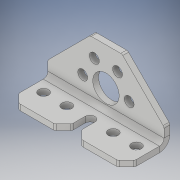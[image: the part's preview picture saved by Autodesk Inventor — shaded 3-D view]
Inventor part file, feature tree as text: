
AUTODESK INVENTOR PART (.ipt)
format: ipt  version: 2018 (Build 220112000, 112)  size: 153,600 bytes
history: native  units: in
note: dims shown in document units (in); Inventor stores cm internally (conversion verified against a paired STEP export)
features: fillet x1
ambient origin geometry x8: Origin, YZ Plane, XZ Plane, XY Plane, X Axis, Y Axis, Z Axis, Center Point
bodies: Solid1 (feature_tree)
feature tree (1):
  fillet  "Fillet3"  [1 undecoded]
note: 1 required parameter value undecoded (feature->parameter linkage not recoverable at this tier; creation-order binding heuristic only, values carry confidence <= 0.55)
